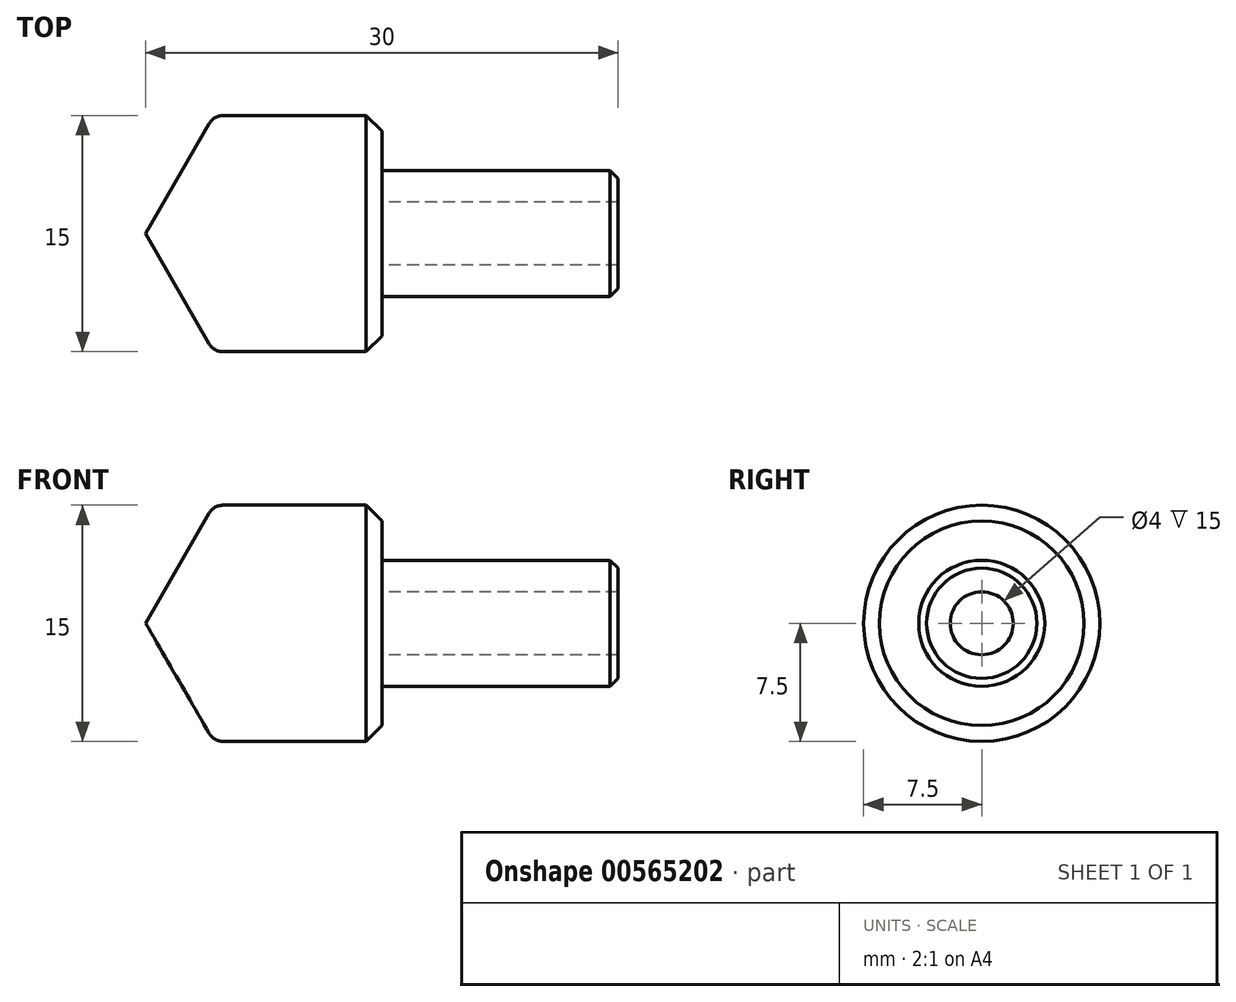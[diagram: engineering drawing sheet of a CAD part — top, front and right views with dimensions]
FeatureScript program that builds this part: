
annotation { "Feature Type Name" : "Feature", "Feature Type Description" : "" }
export const myFeature = defineFeature(function(context is Context, id is Id, definition is map)
    precondition{}
    {
        {
            var Q0;
            Q0=qCreatedBy(makeId("Front.planeOp"),FACE);
            var sketch = newSketch(context, id + "F0", { "sketchPlane" : qUnion([Q0])});
            skLineSegment(sketch, "E0", {"start": v(-10.67, 7.5) * mm, "end": v(0, 7.5) * mm});
            skLineSegment(sketch, "E1", {"start": v(0, 7.5) * mm, "end": v(0, 4) * mm});
            skLineSegment(sketch, "E2", {"start": v(0, 4) * mm, "end": v(15, 4) * mm});
            skLineSegment(sketch, "E3", {"start": v(15, 4) * mm, "end": v(15, 2) * mm});
            skLineSegment(sketch, "E4", {"start": v(-10.67, 7.5) * mm, "end": v(-15, 0) * mm});
            skLineSegment(sketch, "E5", {"start": v(-15, 0) * mm, "end": v(0, 0) * mm});
            skLineSegment(sketch, "E6", {"start": v(0, 0) * mm, "end": v(0, 2) * mm});
            skLineSegment(sketch, "E7", {"start": v(0, 2) * mm, "end": v(15, 2) * mm});
            skPoint(sketch, "E8.orphan", {"position": v(15, 0) * mm});
            skSolve(sketch);
        }
        {
            var Q0;
            Q0=makeQuery(id+"F0.imprint","IMPRINT",FACE,{"disambiguationData":[TD([[makeQuery(id+"F0.imprint","IMPRINT",EDGE,{"derivedFrom":sQuery(id+"F0.wireOp",EDGE,"E0")}),-1.0]])]});
            var Q1;
            Q1=sQuery(id+"F0.wireOp",EDGE,"E5");
            revolve(context, id + "F1", {"entities" : qUnion([Q0]), "axis" : qUnion([Q1]), "revolveType" : RevolveType.FULL});
        }
        {
            var Q0;
            Q0=makeQuery(id+"F1.opRevolve","SWEPT_EDGE",EDGE,{"disambiguationData":[OSD([sQuery(id+"F0.wireOp",EDGE,"E0"),sQuery(id+"F0.wireOp",EDGE,"E4")])]});
            fillet(context, id + "F2", {"entities" : qUnion([Q0]), "radius" : 1 * mm, "tangentPropagation" : true, "allowEdgeOverflow" : false});
        }
        {
            var Q0;
            Q0=makeQuery(id+"F1.opRevolve","SWEPT_EDGE",EDGE,{"disambiguationData":[OSD([sQuery(id+"F0.wireOp",EDGE,"E0"),sQuery(id+"F0.wireOp",EDGE,"E1")])]});
            chamfer(context, id + "F3", {"entities" : qUnion([Q0]), "width" : 1 * mm, "tangentPropagation" : true});
        }
        {
            var Q0;
            Q0=makeQuery(id+"F1.opRevolve","SWEPT_EDGE",EDGE,{"disambiguationData":[OSD([sQuery(id+"F0.wireOp",EDGE,"E2"),sQuery(id+"F0.wireOp",EDGE,"E3")])]});
            chamfer(context, id + "F4", {"entities" : qUnion([Q0]), "width" : .5 * mm, "tangentPropagation" : true});
        }
    });
